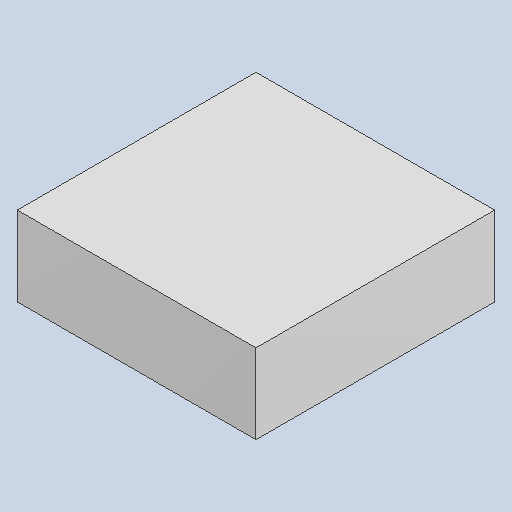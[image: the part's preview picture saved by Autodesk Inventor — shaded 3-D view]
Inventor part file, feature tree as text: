
AUTODESK INVENTOR PART (.ipt)
format: ipt  version: 2023.4 (Build 274418000, 418)  size: 79,872 bytes
history: native  units: mm
features: extrude x1
ambient origin geometry x8: Origin, YZ Plane, XZ Plane, XY Plane, X Axis, Y Axis, Z Axis, Center Point
bodies: Solid1 (feature_tree)
feature tree (1):
  extrude  "Extruded_49"  [1 undecoded]
note: 1 required parameter value undecoded (feature->parameter linkage not recoverable at this tier; creation-order binding heuristic only, values carry confidence <= 0.55)
